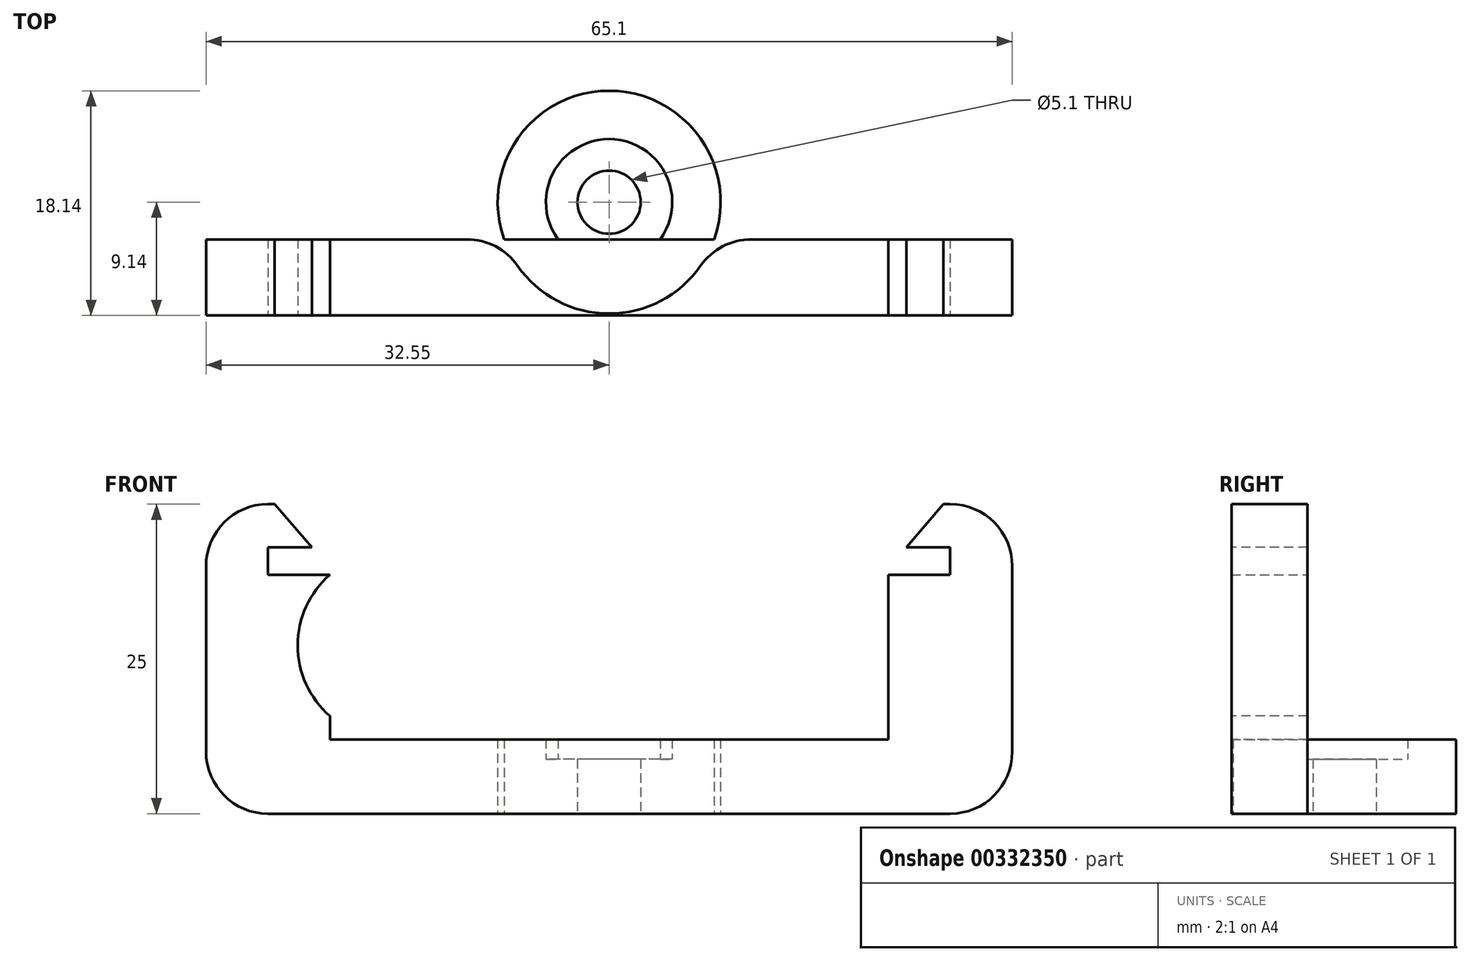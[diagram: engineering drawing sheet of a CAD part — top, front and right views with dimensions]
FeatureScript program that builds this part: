
annotation { "Feature Type Name" : "Feature", "Feature Type Description" : "" }
export const myFeature = defineFeature(function(context is Context, id is Id, definition is map)
    precondition{}
    {
        {
            var Q0;
            Q0=qCreatedBy(makeId("Top.planeOp"),FACE);
            var sketch = newSketch(context, id + "F0", { "sketchPlane" : qUnion([Q0])});
            skCircle(sketch, "E0", {"center": v(0, 0) * mm, "radius": 2.55 * mm});
            skCircle(sketch, "E1", {"center": v(0, 0) * mm, "radius": 5.1 * mm});
            skLineSegment(sketch, "E2.bottom", {"start": v(22.55, -9.14) * mm, "end": v(-22.55, -9.14) * mm});
            skLineSegment(sketch, "E2.top", {"start": v(22.55, -3) * mm, "end": v(-22.55, -3) * mm});
            skLineSegment(sketch, "E2.left", {"start": v(22.55, -9.14) * mm, "end": v(22.55, -3) * mm});
            skPoint(sketch, "E2.middle", {"position": v(0, -6.07) * mm});
            skLineSegment(sketch, "E3.bottom", {"start": v(-22.55, -3) * mm, "end": v(-32.55, -3) * mm});
            skLineSegment(sketch, "E3.top", {"start": v(-22.55, -9.14) * mm, "end": v(-32.55, -9.14) * mm});
            skLineSegment(sketch, "E3.left", {"start": v(-22.55, -3) * mm, "end": v(-22.55, -9.14) * mm});
            skLineSegment(sketch, "E3.right", {"start": v(-32.55, -3) * mm, "end": v(-32.55, -9.14) * mm});
            skLineSegment(sketch, "E4.MirrorCS", {"start": v(22.55, -3) * mm, "end": v(32.55, -3) * mm});
            skLineSegment(sketch, "E5.MirrorCS", {"start": v(32.55, -3) * mm, "end": v(32.55, -9.14) * mm});
            skLineSegment(sketch, "E6.MirrorCS", {"start": v(22.55, -9.14) * mm, "end": v(32.55, -9.14) * mm});
            skCircle(sketch, "E7", {"center": v(0, 0) * mm, "radius": 9 * mm});
            skSolve(sketch);
        }
        {
            var Q0;
            Q0=makeQuery(id+"F0.imprint","IMPRINT",FACE,{"disambiguationData":[TD([[makeQuery(id+"F0.imprint","IMPRINT",EDGE,{"derivedFrom":sQuery(id+"F0.wireOp",EDGE,"E2.bottom")}),-1.0]])]});
            extrude(context, id + "F1", {"entities" : qUnion([Q0]), "depth" : 6 * mm, "offsetDistance" : 25 * mm});
        }
        {
            var Q0;
            Q0=makeQuery(id+"F0.imprint","IMPRINT",FACE,{"disambiguationData":[TD([[makeQuery(id+"F0.imprint","IMPRINT",EDGE,{"derivedFrom":sQuery(id+"F0.wireOp",EDGE,"E3.bottom")}),1.0]])]});
            var Q1;
            Q1=makeQuery(id+"F0.imprint","IMPRINT",FACE,{"disambiguationData":[TD([[makeQuery(id+"F0.imprint","IMPRINT",EDGE,{"derivedFrom":sQuery(id+"F0.wireOp",EDGE,"E2.left")}),-1.0]])]});
            extrude(context, id + "F2", {"entities" : qUnion([Q0, Q1]), "operationType" : NewBodyOperationType.ADD, "depth" : 25 * mm, "offsetDistance" : 25 * mm});
        }
        {
            var Q0;
            {var subQ0=sQuery(id+"F0.wireOp",EDGE,"E2.top");var subQ1=sQuery(id+"F0.wireOp",EDGE,"E1");var subQ2=makeQuery(id+"F0.imprint","INTERSECT",VERTEX,{"disambiguationData":[OD(0.0)],"derivedFrom":[subQ1,subQ0]});Q0=makeQuery(id+"F0.imprint","IMPRINT",FACE,{"disambiguationData":[TD([[makeQuery(id+"F0.imprint","IMPRINT",EDGE,{"disambiguationData":[TD([[subQ2,-1.0]])],"derivedFrom":subQ1}),-1.0]])]});}
            var Q1;
            {var subQ3=sQuery(id+"F0.wireOp",EDGE,"E1");var subQ7=makeQuery(id+"F0.imprint","IMPRINT",VERTEX,{"derivedFrom":subQ3});Q1=makeQuery(id+"F0.imprint","IMPRINT",FACE,{"disambiguationData":[TD([[makeQuery(id+"F0.imprint","IMPRINT",EDGE,{"disambiguationData":[TD([[subQ7,-1.0]])],"derivedFrom":subQ3}),-1.0]])]});}
            extrude(context, id + "F3", {"entities" : qUnion([Q0, Q1]), "operationType" : NewBodyOperationType.ADD, "depth" : 6 * mm, "offsetDistance" : 25 * mm});
        }
        {
            var Q0;
            Q0=makeQuery(id+"F0.imprint","IMPRINT",FACE,{"disambiguationData":[TD([[makeQuery(id+"F0.imprint","IMPRINT",EDGE,{"derivedFrom":sQuery(id+"F0.wireOp",EDGE,"E0")}),-1.0]])]});
            var Q1;
            {var subQ0=sQuery(id+"F0.wireOp",EDGE,"E2.top");var subQ1=sQuery(id+"F0.wireOp",EDGE,"E1");var subQ2=makeQuery(id+"F0.imprint","INTERSECT",VERTEX,{"disambiguationData":[OD(0.0)],"derivedFrom":[subQ1,subQ0]});Q1=makeQuery(id+"F0.imprint","IMPRINT",FACE,{"disambiguationData":[TD([[makeQuery(id+"F0.imprint","IMPRINT",EDGE,{"disambiguationData":[TD([[subQ2,-1.0]])],"derivedFrom":subQ1}),1.0]])]});}
            extrude(context, id + "F4", {"entities" : qUnion([Q0, Q1]), "operationType" : NewBodyOperationType.ADD, "depth" : 4.4 * mm, "offsetDistance" : 25 * mm});
        }
        {
            var Q0;
            {var subQ0=sQuery(id+"F0.wireOp",EDGE,"E7");var subQ1=sQuery(id+"F0.wireOp",EDGE,"E2.top");Q0=makeQuery(id+"F1.opExtrude","SWEPT_EDGE",EDGE,{"disambiguationData":[OSD([subQ1,subQ0]),TDD([makeQuery(id+"F0.imprint","INTERSECT",VERTEX,{"disambiguationData":[OD(1.0)],"derivedFrom":[subQ1,subQ0]})])]});}
            var Q1;
            {var subQ0=sQuery(id+"F0.wireOp",EDGE,"E7");var subQ1=sQuery(id+"F0.wireOp",EDGE,"E2.top");Q1=makeQuery(id+"F1.opExtrude","SWEPT_EDGE",EDGE,{"disambiguationData":[OSD([subQ1,subQ0]),TDD([makeQuery(id+"F0.imprint","INTERSECT",VERTEX,{"disambiguationData":[OD(0.0)],"derivedFrom":[subQ1,subQ0]})])]});}
            var Q2;
            Q2=makeQuery(id+"F1.opExtrude","CAP_EDGE",EDGE,{"disambiguationData":[OSD([sQuery(id+"F0.wireOp",EDGE,"E2.left")])],"isStart":false});
            var Q3;
            Q3=makeQuery(id+"F1.opExtrude","CAP_EDGE",EDGE,{"disambiguationData":[OSD([sQuery(id+"F0.wireOp",EDGE,"E3.left")])],"isStart":false});
            var Q4;
            Q4=makeQuery(id+"F2.opExtrude","CAP_EDGE",EDGE,{"disambiguationData":[OSD([sQuery(id+"F0.wireOp",EDGE,"E3.right")])],"isStart":true});
            var Q5;
            Q5=makeQuery(id+"F2.opExtrude","CAP_EDGE",EDGE,{"disambiguationData":[OSD([sQuery(id+"F0.wireOp",EDGE,"E5.MirrorCS")])],"isStart":true});
            var Q6;
            Q6=makeQuery(id+"F2.opExtrude","CAP_EDGE",EDGE,{"disambiguationData":[OSD([sQuery(id+"F0.wireOp",EDGE,"E5.MirrorCS")])],"isStart":false});
            var Q7;
            Q7=makeQuery(id+"F2.opExtrude","CAP_EDGE",EDGE,{"disambiguationData":[OSD([sQuery(id+"F0.wireOp",EDGE,"E3.right")])],"isStart":false});
            fillet(context, id + "F5", {"entities" : qUnion([Q0, Q1, Q2, Q3, Q4, Q5, Q6, Q7]), "tangentPropagation" : true, "radius" : 5 * mm, "defaultsChanged" : false, "vertexSettings" : [], "allowEdgeOverflow" : false});
        }
        {
            var Q0;
            Q0=makeQuery(id+"F2.boolean.opBoolean","MERGE",FACE,{"derivedFrom":[makeQuery(id+"F1.opExtrude","SWEPT_FACE",FACE,{"disambiguationData":[OSD([sQuery(id+"F0.wireOp",EDGE,"E2.bottom")])]}),makeQuery(id+"F2.opExtrude","SWEPT_FACE",FACE,{"disambiguationData":[OSD([sQuery(id+"F0.wireOp",EDGE,"E3.top")])]}),makeQuery(id+"F2.opExtrude","SWEPT_FACE",FACE,{"disambiguationData":[OSD([sQuery(id+"F0.wireOp",EDGE,"E6.MirrorCS")])]})]});
            var sketch = newSketch(context, id + "F6", { "sketchPlane" : qUnion([Q0])});
            skLineSegment(sketch, "E8.bottom", {"start": v(27.55, 19.3) * mm, "end": v(-27.55, 19.3) * mm});
            skLineSegment(sketch, "E8.top", {"start": v(27.55, 21.5) * mm, "end": v(-27.55, 21.5) * mm});
            skLineSegment(sketch, "E8.left", {"start": v(27.55, 19.3) * mm, "end": v(27.55, 21.5) * mm});
            skLineSegment(sketch, "E8.right", {"start": v(-27.55, 19.3) * mm, "end": v(-27.55, 21.5) * mm});
            skPoint(sketch, "E8.middle", {"position": v(0, 20.4) * mm});
            skLineSegment(sketch, "E9", {"start": v(-27, 25) * mm, "end": v(-24, 21.5) * mm});
            skLineSegment(sketch, "E10.MirrorCS", {"start": v(27, 25) * mm, "end": v(24, 21.5) * mm});
            skLineSegment(sketch, "E11", {"start": v(-27, 25) * mm, "end": v(27, 25) * mm});
            skArc(sketch, "E12", {"start": v(-22.55, 19.3) * mm, "mid": v(-24.65, 10.92) * mm, "end": v(-17.55, 6) * mm});
            skLineSegment(sketch, "E13", {"start": v(-17.55, 6) * mm, "end": v(-17.55, 19.3) * mm});
            skArc(sketch, "E14.MirrorCS", {"start": v(22.55, 19.3) * mm, "mid": v(24.65, 10.92) * mm, "end": v(17.55, 6) * mm});
            skLineSegment(sketch, "E15.MirrorCS", {"start": v(17.55, 6) * mm, "end": v(17.55, 19.3) * mm});
            skSolve(sketch);
        }
        {
            var Q0;
            {var subQ0=sQuery(id+"F6.wireOp",EDGE,"E8.bottom");var subQ1=sQuery(id+"F0.wireOp",EDGE,"E2.bottom");var subQ2=makeQuery(id+"F2.opExtrude","SWEPT_EDGE",EDGE,{"disambiguationData":[OSD([subQ1,sQuery(id+"F0.wireOp",EDGE,"E2.left"),sQuery(id+"F0.wireOp",EDGE,"E6.MirrorCS")])]});var subQ3=makeQuery(id+"F6.imprint","INTERSECT",VERTEX,{"derivedFrom":[subQ2,subQ0]});Q0=makeQuery(id+"F6.imprint","IMPRINT",FACE,{"disambiguationData":[TD([[makeQuery(id+"F6.imprint","IMPRINT",EDGE,{"disambiguationData":[TD([[subQ3,-1.0]])],"derivedFrom":subQ0}),-1.0]])]});}
            var Q1;
            {var subQ0=sQuery(id+"F6.wireOp",EDGE,"E8.right");Q1=makeQuery(id+"F6.imprint","IMPRINT",FACE,{"disambiguationData":[TD([[makeQuery(id+"F6.imprint","IMPRINT",EDGE,{"derivedFrom":subQ0}),-1.0]])]});}
            var Q2;
            {var subQ0=sQuery(id+"F6.wireOp",EDGE,"E8.left");Q2=makeQuery(id+"F6.imprint","IMPRINT",FACE,{"disambiguationData":[TD([[makeQuery(id+"F6.imprint","IMPRINT",EDGE,{"derivedFrom":subQ0}),1.0]])]});}
            var Q3;
            {var subQ0=sQuery(id+"F6.wireOp",EDGE,"E9");Q3=makeQuery(id+"F6.imprint","IMPRINT",FACE,{"disambiguationData":[TD([[makeQuery(id+"F6.imprint","IMPRINT",EDGE,{"derivedFrom":subQ0}),1.0]])]});}
            var Q4;
            {var subQ0=sQuery(id+"F6.wireOp",EDGE,"E10.MirrorCS");Q4=makeQuery(id+"F6.imprint","IMPRINT",FACE,{"disambiguationData":[TD([[makeQuery(id+"F6.imprint","IMPRINT",EDGE,{"derivedFrom":subQ0}),-1.0]])]});}
            var Q5;
            {var subQ0=sQuery(id+"F6.wireOp",EDGE,"E12");Q5=makeQuery(id+"F6.imprint","IMPRINT",FACE,{"disambiguationData":[TD([[makeQuery(id+"F6.imprint","IMPRINT",EDGE,{"derivedFrom":subQ0}),1.0]])]});}
            var Q6;
            {var subQ0=sQuery(id+"F6.wireOp",EDGE,"E14.MirrorCS");Q6=makeQuery(id+"F6.imprint","IMPRINT",FACE,{"disambiguationData":[TD([[makeQuery(id+"F6.imprint","IMPRINT",EDGE,{"derivedFrom":subQ0}),-1.0]])]});}
            extrude(context, id + "F7", {"entities" : qUnion([Q0, Q1, Q2, Q3, Q4, Q5, Q6]), "operationType" : NewBodyOperationType.REMOVE, "oppositeDirection" : true, "depth" : 10 * mm, "offsetDistance" : 25 * mm});
        }
    });
